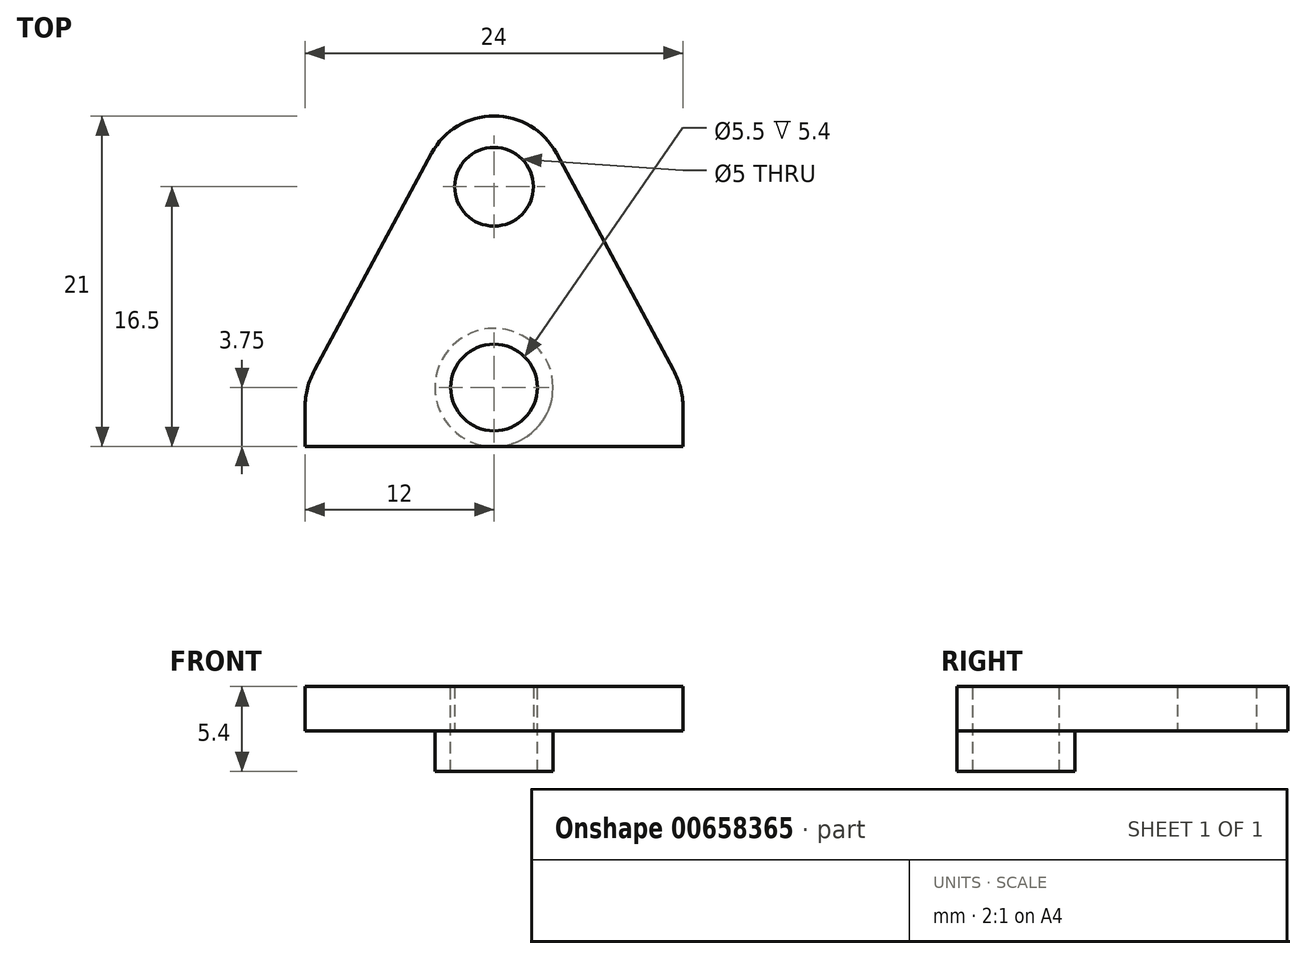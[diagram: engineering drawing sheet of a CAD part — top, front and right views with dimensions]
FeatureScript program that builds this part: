
annotation { "Feature Type Name" : "Feature", "Feature Type Description" : "" }
export const myFeature = defineFeature(function(context is Context, id is Id, definition is map)
    precondition{}
    {
        {
            var Q0;
            Q0=qCreatedBy(makeId("Top.planeOp"),FACE);
            var sketch = newSketch(context, id + "F0", { "sketchPlane" : qUnion([Q0])});
            skCircle(sketch, "E0", {"center": v(0, 0) * mm, "radius": 3.75 * mm});
            skCircle(sketch, "E1", {"center": v(0, 0) * mm, "radius": 2.75 * mm});
            skSolve(sketch);
        }
        {
            var Q0;
            Q0=makeQuery(id+"F0.imprint","IMPRINT",FACE,{"disambiguationData":[TD([[makeQuery(id+"F0.imprint","IMPRINT",EDGE,{"derivedFrom":sQuery(id+"F0.wireOp",EDGE,"E0")}),1.0]])]});
            extrude(context, id + "F1", {"entities" : qUnion([Q0]), "oppositeDirection" : true, "depth" : 2.6 * mm, "offsetDistance" : 25 * mm});
        }
        {
            var Q0;
            Q0=qCreatedBy(makeId("Top.planeOp"),FACE);
            var sketch = newSketch(context, id + "F2", { "sketchPlane" : qUnion([Q0])});
            skCircle(sketch, "E2.0", {"center": v(0, 0) * mm, "radius": 2.75 * mm});
            skCircle(sketch, "E3.0", {"center": v(0, 0) * mm, "radius": 3.75 * mm, "construction": true});
            skLineSegment(sketch, "E4.bottom", {"start": v(12, -3.75) * mm, "end": v(-12, -3.75) * mm});
            skLineSegment(sketch, "E4.left", {"start": v(12, -3.75) * mm, "end": v(12, -1.26) * mm});
            skLineSegment(sketch, "E4.right", {"start": v(-12, -3.75) * mm, "end": v(-12, -1.26) * mm});
            skPoint(sketch, "E4.middle", {"position": v(0, -1.88) * mm});
            skLineSegment(sketch, "E5", {"start": v(-11.4, 1.11) * mm, "end": v(-3.96, 14.89) * mm});
            skLineSegment(sketch, "E6", {"start": v(3.96, 14.89) * mm, "end": v(11.4, 1.11) * mm});
            skLineSegment(sketch, "E7", {"start": v(-12, 8.25) * mm, "end": v(12, 8.25) * mm, "construction": true});
            skCircle(sketch, "E8", {"center": v(0, 12.75) * mm, "radius": 2.5 * mm});
            skArc(sketch, "E9", {"start": v(-3.96, 14.89) * mm, "mid": v(0, 8.25) * mm, "end": v(3.96, 14.89) * mm, "construction": true});
            skArc(sketch, "E10", {"start": v(3.96, 14.89) * mm, "mid": v(0, 17.25) * mm, "end": v(-3.96, 14.89) * mm});
            skPoint(sketch, "E11.visualSharp", {"position": v(-12, 0) * mm});
            skArc(sketch, "E11.filletArc", {"start": v(-11.4, 1.11) * mm, "mid": v(-11.85, -0.04) * mm, "end": v(-12, -1.26) * mm});
            skPoint(sketch, "E12.visualSharp", {"position": v(12, 0) * mm});
            skArc(sketch, "E12.filletArc", {"start": v(12, -1.26) * mm, "mid": v(11.85, -0.04) * mm, "end": v(11.4, 1.11) * mm});
            skSolve(sketch);
        }
        {
            var Q0;
            Q0=makeQuery(id+"F2.imprint","IMPRINT",FACE,{"disambiguationData":[TD([[makeQuery(id+"F2.imprint","IMPRINT",EDGE,{"derivedFrom":sQuery(id+"F2.wireOp",EDGE,"E2.0")}),-1.0]])]});
            extrude(context, id + "F3", {"entities" : qUnion([Q0]), "operationType" : NewBodyOperationType.ADD, "depth" : 2.8 * mm, "offsetDistance" : 25 * mm});
        }
    });
